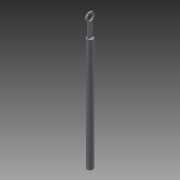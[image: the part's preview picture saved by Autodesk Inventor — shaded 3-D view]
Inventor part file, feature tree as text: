
AUTODESK INVENTOR PART (.ipt)
format: ipt  version: 2015 SP1 (Build 190203100, 203)  size: 116,736 bytes
history: native  units: in
note: dims shown in document units (in); Inventor stores cm internally (conversion verified against a paired STEP export)
features: sketch x4, extrude x3, projected_geometry x2, revolve x1
ambient origin geometry x8: Origin, YZ Plane, XZ Plane, XY Plane, X Axis, Y Axis, Z Axis, Center Point
bodies: Solid1 (feature_tree)
feature tree (10):
  revolve  "Revolution1"  Angle=90.0deg
  extrude  "Extrusion1"  Depth=3.75in
  extrude  "Extrusion2"  Depth=1.5in
  extrude  "Extrusion3"  Depth=0.25in TaperAngle=0.0deg
  sketch  "Sketch1"  dims[d0=19.0in d6=90.0deg]
  sketch  "Sketch2"  dims[d8=3.75in d9=0.0in d10=3.0in]
  sketch  "Sketch3"  dims[d11=1.0in d12=1.5in]
  projected_geometry  "Projected Loop1"
  sketch  "Sketch4"  dims[d13=0.25in d14=0.0in d15=0.25in d16=0.0in]
  projected_geometry  "Projected Loop2"
